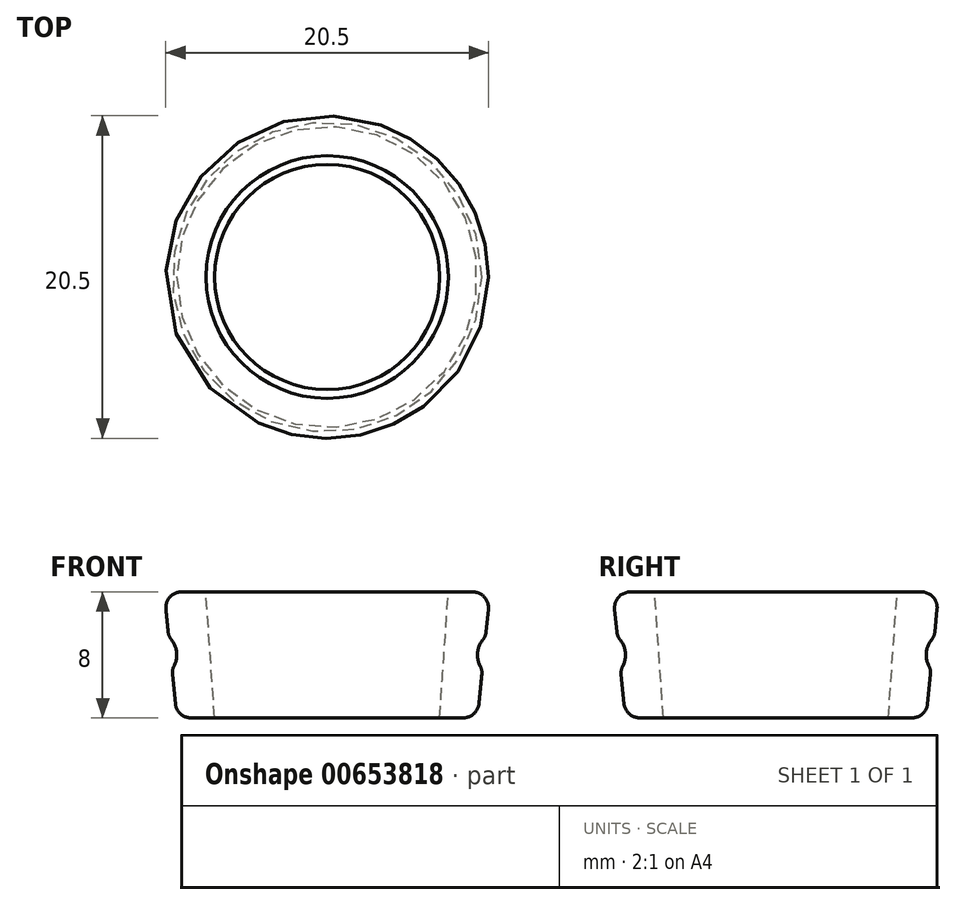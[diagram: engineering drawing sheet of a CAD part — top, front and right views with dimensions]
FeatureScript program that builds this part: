
annotation { "Feature Type Name" : "Feature", "Feature Type Description" : "" }
export const myFeature = defineFeature(function(context is Context, id is Id, definition is map)
    precondition{}
    {
        {
            var Q0;
            Q0=qCreatedBy(makeId("Top.planeOp"),FACE);
            var sketch = newSketch(context, id + "F0", { "sketchPlane" : qUnion([Q0])});
            skCircle(sketch, "E0", {"center": v(0, 0) * mm, "radius": 9.55 * mm, "construction": true});
            skCircle(sketch, "E1", {"center": v(0, 0) * mm, "radius": 12.55 * mm, "construction": true});
            skCircle(sketch, "E2", {"center": v(0, 0) * mm, "radius": 11.05 * mm});
            skLineSegment(sketch, "E3", {"start": v(-12.55, 0) * mm, "end": v(-11.05, 0) * mm, "construction": true});
            skLineSegment(sketch, "E4", {"start": v(-11.05, 0) * mm, "end": v(-9.55, 0) * mm, "construction": true});
            skSolve(sketch);
        }
        {
            var Q0;
            Q0=qCreatedBy(makeId("Front.planeOp"),FACE);
            var sketch = newSketch(context, id + "F1", { "sketchPlane" : qUnion([Q0])});
            skPoint(sketch, "E5.0", {"position": v(-11.05, 0) * mm});
            skPoint(sketch, "E6.0", {"position": v(-9.55, 0) * mm});
            skCircle(sketch, "E7", {"center": v(-11.05, 0) * mm, "radius": 1.5 * mm});
            skSolve(sketch);
        }
        {
            var Q0;
            Q0=makeQuery(id+"F1.imprint","IMPRINT",FACE,{"disambiguationData":[TD([[makeQuery(id+"F1.imprint","IMPRINT",EDGE,{"derivedFrom":sQuery(id+"F1.wireOp",EDGE,"E7")}),1.0]])]});
            var Q1;
            Q1=sQuery(id+"F0.wireOp",EDGE,"E2");
            revolve(context, id + "F2", {"entities" : qUnion([Q0]), "axis" : qUnion([Q1]), "revolveType" : RevolveType.FULL});
        }
        {
            var Q0;
            Q0=qCreatedBy(makeId("Top.planeOp"),FACE);
            cPlane(context, id + "F3", {"entities" : qUnion([Q0]), "cplaneType" : CPlaneType.OFFSET, "offset" : 4 * mm, "width" : 150 * mm, "height" : 150 * mm});
        }
        {
            var Q0;
            Q0=qCreatedBy(makeId("Top.planeOp"),FACE);
            cPlane(context, id + "F4", {"entities" : qUnion([Q0]), "cplaneType" : CPlaneType.OFFSET, "offset" : 4 * mm, "oppositeDirection" : true, "width" : 150 * mm, "height" : 150 * mm});
        }
        {
            var Q0;
            Q0=qCreatedBy(id+"F4.planeOp",FACE);
            var sketch = newSketch(context, id + "F5", { "sketchPlane" : qUnion([Q0])});
            skCircle(sketch, "E8", {"center": v(0, 0) * mm, "radius": 7.15 * mm, "construction": true});
            skCircle(sketch, "E9", {"center": v(0, 0) * mm, "radius": 9.55 * mm});
            skSolve(sketch);
        }
        {
            var Q0;
            Q0=qCreatedBy(id+"F3.planeOp",FACE);
            var sketch = newSketch(context, id + "F6", { "sketchPlane" : qUnion([Q0])});
            skCircle(sketch, "E10", {"center": v(0, 0) * mm, "radius": 7.7 * mm, "construction": true});
            skCircle(sketch, "E11", {"center": v(0, 0) * mm, "radius": 10.35 * mm});
            skCircle(sketch, "E12", {"center": v(0, 0) * mm, "radius": 9.55 * mm, "construction": true});
            skSolve(sketch);
        }
        {
            var Q0;
            Q0 = qSketchRegion(id + "F5", true);
            var Q1;
            Q1 = qSketchRegion(id + "F6", true);
            loft(context, id + "F7", {"sheetProfilesArray" : [{ "sheetProfileEntities" : qUnion([Q0]) }, { "sheetProfileEntities" : qUnion([Q1]) }]});
        }
        {
            var Q0;
            Q0=makeQuery(id+"F6.imprint","IMPRINT",FACE,{"disambiguationData":[TD([[makeQuery(id+"F6.imprint","IMPRINT",EDGE,{"derivedFrom":sQuery(id+"F6.wireOp",EDGE,"E11")}),1.0]])]});
            var sketch = newSketch(context, id + "F8", { "sketchPlane" : qUnion([Q0])});
            skCircle(sketch, "E13.0", {"center": v(0, 0) * mm, "radius": 7.7 * mm});
            skSolve(sketch);
        }
        {
            var Q0;
            Q0=makeQuery(id+"F5.imprint","IMPRINT",FACE,{"disambiguationData":[TD([[makeQuery(id+"F5.imprint","IMPRINT",EDGE,{"derivedFrom":sQuery(id+"F5.wireOp",EDGE,"E9")}),1.0]])]});
            var sketch = newSketch(context, id + "F9", { "sketchPlane" : qUnion([Q0])});
            skCircle(sketch, "E14.0", {"center": v(0, 0) * mm, "radius": 7.15 * mm});
            skSolve(sketch);
        }
        {
            var Q1;
            Q1 = qSketchRegion(id + "F8", true);
            var Q2;
            Q2 = qSketchRegion(id + "F9", true);
            loft(context, id + "F10", {"operationType" : NewBodyOperationType.REMOVE, "sheetProfilesArray" : [{ "sheetProfileEntities" : qUnion([Q1]) }, { "sheetProfileEntities" : qUnion([Q2]) }]});
        }
        {
            var Q0;
            Q0=makeQuery(id+"F2.opRevolve","SWEPT_BODY",BODY,{"disambiguationData":[OSD([sQuery(id+"F1.wireOp",EDGE,"E7")])]});
            var Q1;
            Q1=makeQuery(id+"F7.opLoft","SWEPT_BODY",BODY,{"disambiguationData":[OSD([makeQuery(id+"F5.imprint","IMPRINT",FACE,{"disambiguationData":[TD([[makeQuery(id+"F5.imprint","IMPRINT",EDGE,{"derivedFrom":sQuery(id+"F5.wireOp",EDGE,"E9")}),1.0]])]}),makeQuery(id+"F6.imprint","IMPRINT",FACE,{"disambiguationData":[TD([[makeQuery(id+"F6.imprint","IMPRINT",EDGE,{"derivedFrom":sQuery(id+"F6.wireOp",EDGE,"E11")}),1.0]])]})])]});
            booleanBodies(context, id + "F11", {"operationType" : BooleanOperationType.SUBTRACTION, "tools" : qUnion([Q0]), "targets" : qUnion([Q1])});
        }
        {
            var Q0;
            Q0=makeQuery(id+"F10.boolean.opBoolean","COPY",EDGE,{"derivedFrom":makeQuery(id+"F10.opLoft","MID_CAP_EDGE",EDGE,{"disambiguationData":[OSD([sQuery(id+"F8.wireOp",EDGE,"E13.0")])],"capPos":0.0})});
            var Q1;
            Q1=makeQuery(id+"F7.opLoft","MID_CAP_EDGE",EDGE,{"disambiguationData":[OSD([sQuery(id+"F5.wireOp",EDGE,"E9"),sQuery(id+"F6.wireOp",EDGE,"E11")])],"capPos":1.0});
            var Q2;
            Q2=makeQuery(id+"F11.opBoolean","INTERSECT",EDGE,{"disambiguationData":[OD(1.0)],"derivedFrom":[makeQuery(id+"F2.opRevolve","SWEPT_FACE",FACE,{"disambiguationData":[OSD([sQuery(id+"F1.wireOp",EDGE,"E7")])]}),makeQuery(id+"F7.opLoft","SWEPT_FACE",FACE,{"disambiguationData":[OSD([sQuery(id+"F5.wireOp",EDGE,"E9"),sQuery(id+"F6.wireOp",EDGE,"E11")])]})]});
            var Q3;
            Q3=makeQuery(id+"F11.opBoolean","INTERSECT",EDGE,{"disambiguationData":[OD(0.0)],"derivedFrom":[makeQuery(id+"F2.opRevolve","SWEPT_FACE",FACE,{"disambiguationData":[OSD([sQuery(id+"F1.wireOp",EDGE,"E7")])]}),makeQuery(id+"F7.opLoft","SWEPT_FACE",FACE,{"disambiguationData":[OSD([sQuery(id+"F5.wireOp",EDGE,"E9"),sQuery(id+"F6.wireOp",EDGE,"E11")])]})]});
            var Q4;
            Q4=makeQuery(id+"F7.opLoft","MID_CAP_EDGE",EDGE,{"disambiguationData":[OSD([sQuery(id+"F5.wireOp",EDGE,"E9")])],"capPos":0.0});
            var Q5;
            Q5=makeQuery(id+"F10.boolean.opBoolean","COPY",EDGE,{"derivedFrom":makeQuery(id+"F10.opLoft","MID_CAP_EDGE",EDGE,{"disambiguationData":[OSD([sQuery(id+"F8.wireOp",EDGE,"E13.0"),sQuery(id+"F9.wireOp",EDGE,"E14.0")])],"capPos":1.0})});
            fillet(context, id + "F12", {"entities" : qUnion([Q0, Q1, Q2, Q3, Q4, Q5]), "radius" : 1 * mm, "tangentPropagation" : true, "allowEdgeOverflow" : false});
        }
    });
